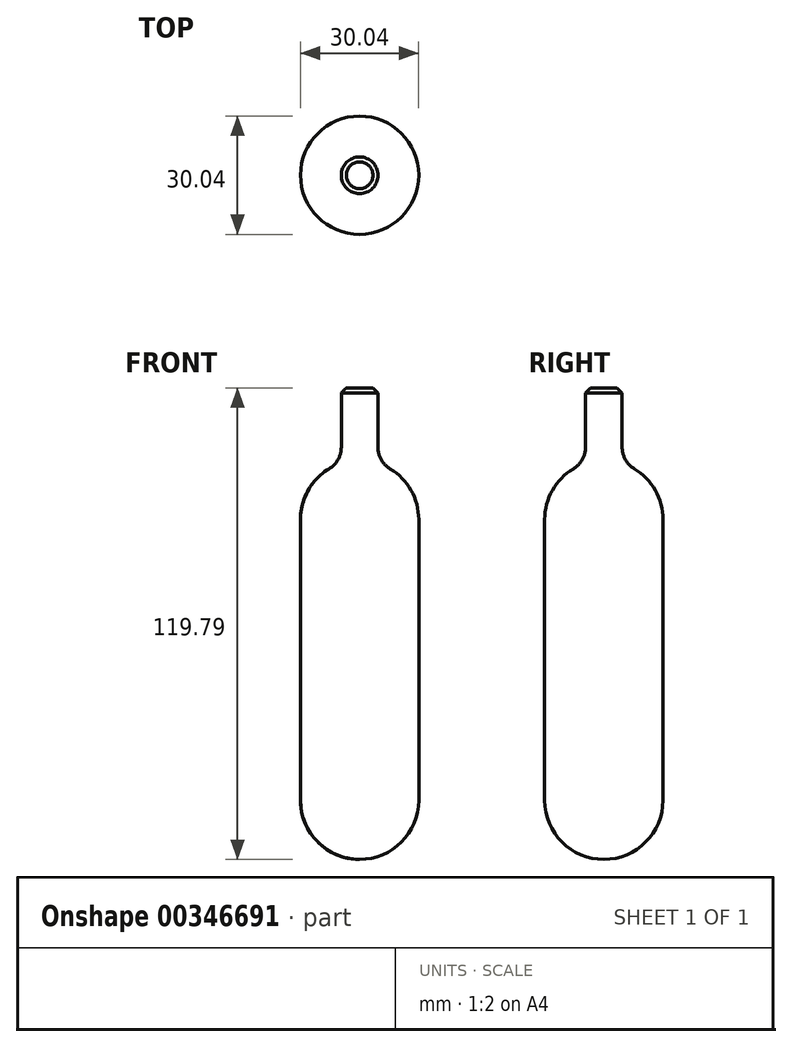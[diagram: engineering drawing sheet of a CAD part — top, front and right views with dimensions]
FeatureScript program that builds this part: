
annotation { "Feature Type Name" : "Feature", "Feature Type Description" : "" }
export const myFeature = defineFeature(function(context is Context, id is Id, definition is map)
    precondition{}
    {
        {
            var Q0;
            Q0=qCreatedBy(makeId("Front.planeOp"),FACE);
            var sketch = newSketch(context, id + "F0", { "sketchPlane" : qUnion([Q0])});
            skLineSegment(sketch, "E0", {"start": v(0, 0) * mm, "end": v(0, 119.79) * mm});
            skLineSegment(sketch, "E1", {"start": v(0, 0) * mm, "end": v(0, 15.02) * mm});
            skArc(sketch, "E2", {"start": v(0, 0) * mm, "mid": v(10.62, 4.4) * mm, "end": v(15.02, 15.02) * mm});
            skLineSegment(sketch, "E3", {"start": v(0, 0) * mm, "end": v(0, 86.36) * mm});
            skArc(sketch, "E4", {"start": v(15.02, 86.36) * mm, "mid": v(13.08, 93.76) * mm, "end": v(7.74, 99.24) * mm});
            skLineSegment(sketch, "E5", {"start": v(0, 15.02) * mm, "end": v(15.02, 15.02) * mm});
            skLineSegment(sketch, "E6", {"start": v(15.02, 15.02) * mm, "end": v(15.02, 86.36) * mm});
            skLineSegment(sketch, "E7", {"start": v(0, 119.79) * mm, "end": v(4.66, 119.79) * mm});
            skLineSegment(sketch, "E8", {"start": v(4.66, 119.79) * mm, "end": v(4.66, 104.68) * mm});
            skPoint(sketch, "E9.visualSharp", {"position": v(4.66, 100.64) * mm});
            skArc(sketch, "E9.filletArc", {"start": v(4.66, 104.68) * mm, "mid": v(5.48, 101.55) * mm, "end": v(7.74, 99.24) * mm});
            skSolve(sketch);
        }
        {
            var Q0;
            Q0 = qSketchRegion(id + "F0", true);
            var Q1;
            Q1=sQuery(id+"F0.wireOp",EDGE,"E3");
            revolve(context, id + "F1", {"entities" : qUnion([Q0]), "axis" : qUnion([Q1]), "revolveType" : RevolveType.FULL});
        }
        {
            var Q0;
            Q0=makeQuery(id+"F1.opRevolve","SWEPT_EDGE",EDGE,{"disambiguationData":[OSD([sQuery(id+"F0.wireOp",EDGE,"E7"),sQuery(id+"F0.wireOp",EDGE,"E8")])]});
            chamfer(context, id + "F2", {"entities" : qUnion([Q0]), "width" : 1.27 * mm, "tangentPropagation" : true});
        }
    });
